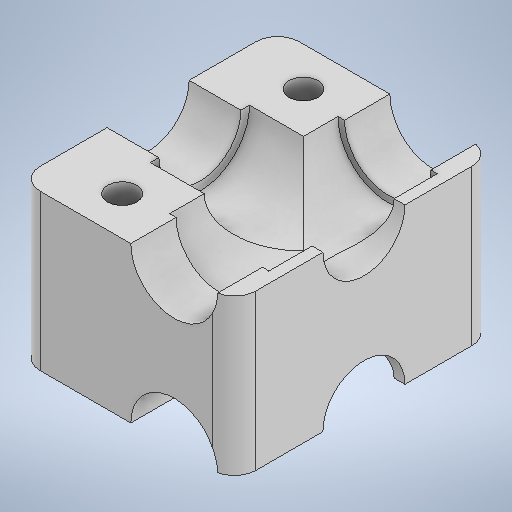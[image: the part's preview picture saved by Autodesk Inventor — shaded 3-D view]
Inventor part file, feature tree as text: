
AUTODESK INVENTOR PART (.ipt)
format: ipt  version: 2025 (Build 290162000, 162)  size: 307,200 bytes
history: native  units: mm
features: sketch x6, extrude x5, plane x1, hole x1, fillet x1, mirror x1
ambient origin geometry x8: Origin, YZ Plane, XZ Plane, XY Plane, X Axis, Y Axis, Z Axis, Center Point
bodies: Solid1 (feature_tree)
feature tree (15):
  extrude  "Extrusion1"  Depth=60.0mm
  extrude  "Extrusion2"  Depth=18.0mm
  extrude  "Extrusion3"  Depth=20.0mm
  extrude  "Extrusion4"  TaperAngle=0.0deg  [1 undecoded]
  plane  "Work Plane2"
  extrude  "Extrusion5"  Depth=39.0mm TaperAngle=0.0deg
  hole  "Hole2"  [1 undecoded]
  fillet  "Fillet1"  Radius=9.0mm
  mirror  "Mirror1"
  sketch  "Sketch1"  dims[d0=50.0mm d1=60.0mm]
  sketch  "Sketch2"  dims[d2=18.0mm d3=0.0mm d4=19.0mm]
  sketch  "Sketch3"  dims[d5=0.0mm d6=0.0mm d7=20.0mm]
  sketch  "Sketch4"  dims[d8=14.0mm d9=0.0mm d10=0.0mm]
  sketch  "Sketch5"  dims[d11=23.0mm d12=39.0mm d13=0.0mm]
  sketch  "Sketch7"  dims[d14=23.0mm d15=24.0mm d16=0.0mm d28=9.0mm d29=9.0mm d30=15.0mm d31=6.756mm d32=6.0mm d33=11.113mm d34=6.35mm d35=90.0deg d36=8.0mm d37=20.594885mm d38=5.0mm]
note: 2 required parameter values undecoded (feature->parameter linkage not recoverable at this tier; creation-order binding heuristic only, values carry confidence <= 0.55)
